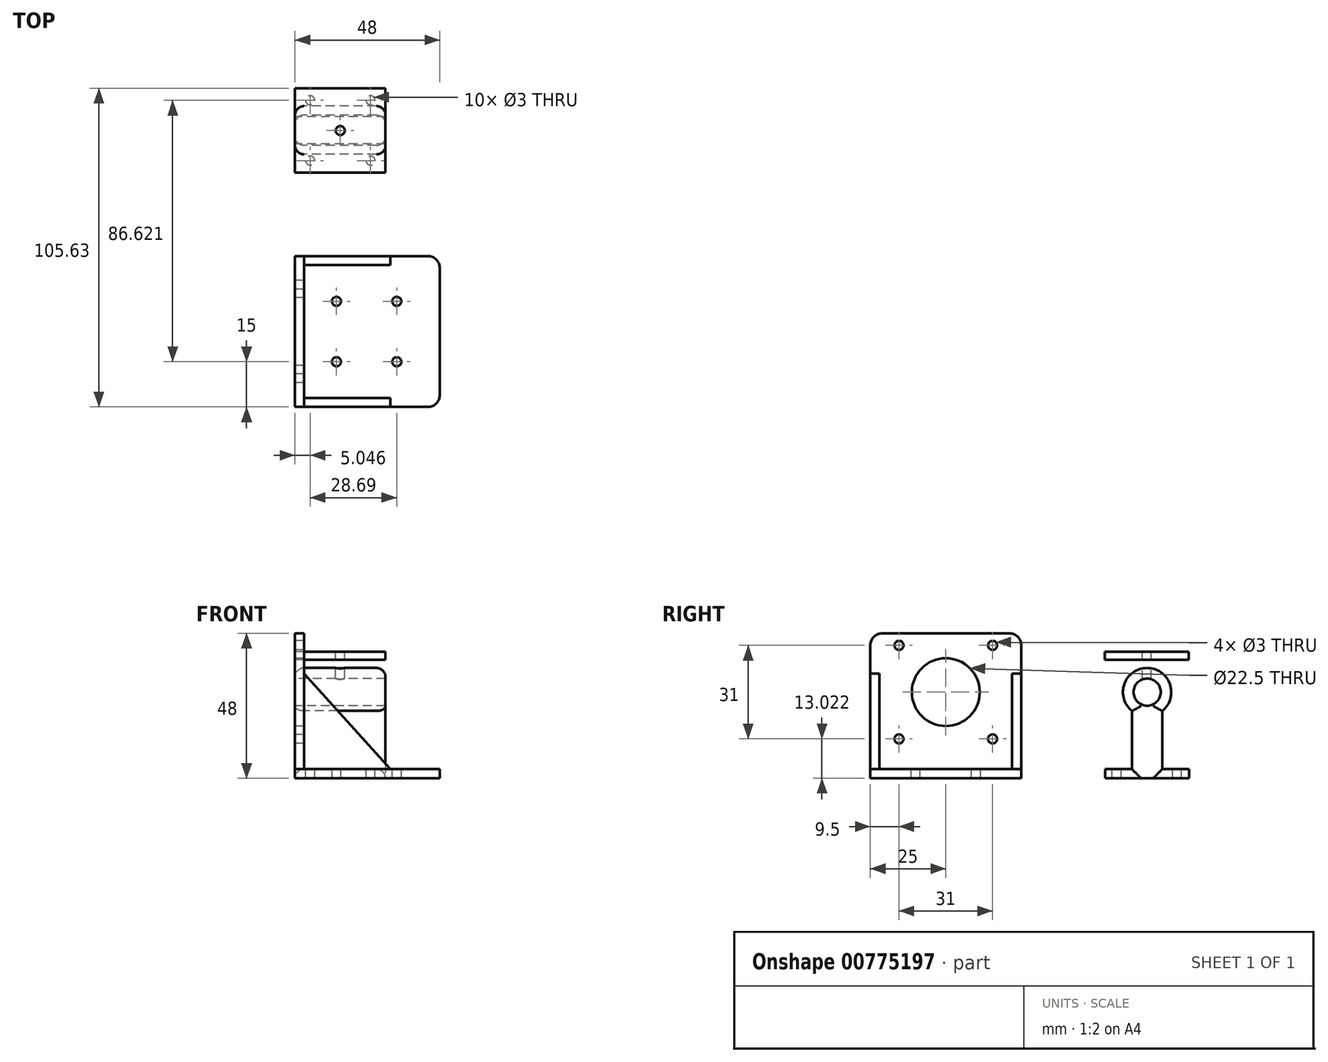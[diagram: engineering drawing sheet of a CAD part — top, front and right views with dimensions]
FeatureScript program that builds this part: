
annotation { "Feature Type Name" : "Feature", "Feature Type Description" : "" }
export const myFeature = defineFeature(function(context is Context, id is Id, definition is map)
    precondition{}
    {
        {
            var Q0;
            Q0=qCreatedBy(makeId("Right.planeOp"),FACE);
            var sketch = newSketch(context, id + "F0", { "sketchPlane" : qUnion([Q0])});
            skLineSegment(sketch, "E0.bottom", {"start": v(-50, 48) * mm, "end": v(0, 48) * mm});
            skLineSegment(sketch, "E0.top", {"start": v(-50, 0) * mm, "end": v(0, 0) * mm});
            skLineSegment(sketch, "E0.left", {"start": v(-50, 48) * mm, "end": v(-50, 0) * mm});
            skLineSegment(sketch, "E0.right", {"start": v(0, 48) * mm, "end": v(0, 0) * mm});
            skLineSegment(sketch, "E1.bottom", {"start": v(-46, 48) * mm, "end": v(-4, 48) * mm, "construction": true});
            skLineSegment(sketch, "E1.top", {"start": v(-46, 9.04) * mm, "end": v(-4, 9.04) * mm, "construction": true});
            skLineSegment(sketch, "E1.left", {"start": v(-46, 48) * mm, "end": v(-46, 9.04) * mm, "construction": true});
            skLineSegment(sketch, "E1.right", {"start": v(-4, 48) * mm, "end": v(-4, 9.04) * mm, "construction": true});
            skPoint(sketch, "E2", {"position": v(-25, 48) * mm});
            skLineSegment(sketch, "E3.bottom", {"start": v(-40.5, 44.02) * mm, "end": v(-9.5, 44.02) * mm, "construction": true});
            skLineSegment(sketch, "E3.top", {"start": v(-40.5, 13.02) * mm, "end": v(-9.5, 13.02) * mm, "construction": true});
            skLineSegment(sketch, "E3.left", {"start": v(-40.5, 44.02) * mm, "end": v(-40.5, 13.02) * mm, "construction": true});
            skLineSegment(sketch, "E3.right", {"start": v(-9.5, 44.02) * mm, "end": v(-9.5, 13.02) * mm, "construction": true});
            skPoint(sketch, "E4", {"position": v(-25, 44.02) * mm});
            skLineSegment(sketch, "E5", {"start": v(-40.5, 44.02) * mm, "end": v(-9.5, 13.02) * mm, "construction": true});
            skLineSegment(sketch, "E6", {"start": v(-9.5, 44.02) * mm, "end": v(-40.5, 13.02) * mm, "construction": true});
            skPoint(sketch, "E7", {"position": v(-25, 28.52) * mm});
            skLineSegment(sketch, "E8.top", {"start": v(-50, 3) * mm, "end": v(0, 3) * mm});
            skLineSegment(sketch, "E8.left", {"start": v(-50, 0) * mm, "end": v(-50, 3) * mm});
            skLineSegment(sketch, "E8.right", {"start": v(0, 0) * mm, "end": v(0, 3) * mm});
            skLineSegment(sketch, "E9", {"start": v(-25, 28.52) * mm, "end": v(41.7, 28.52) * mm, "construction": true});
            skCircle(sketch, "E10", {"center": v(41.7, 28.52) * mm, "radius": 8 * mm});
            skCircle(sketch, "E11", {"center": v(41.7, 28.52) * mm, "radius": 4.5 * mm});
            skLineSegment(sketch, "E12", {"start": v(41.7, 44.02) * mm, "end": v(41.7, 0) * mm, "construction": true});
            skLineSegment(sketch, "E13", {"start": v(36.7, 22.29) * mm, "end": v(36.7, 3) * mm});
            skLineSegment(sketch, "E14.left", {"start": v(41.7, 0) * mm, "end": v(41.7, 0) * mm});
            skLineSegment(sketch, "E15.bottom", {"start": v(41.7, 0) * mm, "end": v(27.8, 0) * mm});
            skLineSegment(sketch, "E15.top", {"start": v(41.7, 3) * mm, "end": v(27.8, 3) * mm});
            skLineSegment(sketch, "E15.left", {"start": v(41.7, 0) * mm, "end": v(41.7, 3) * mm});
            skLineSegment(sketch, "E15.right", {"start": v(27.8, 0) * mm, "end": v(27.8, 3) * mm});
            skLineSegment(sketch, "E16.MirrorCS", {"start": v(41.7, 0) * mm, "end": v(55.63, 0) * mm});
            skLineSegment(sketch, "E17.MirrorCS", {"start": v(55.63, 0) * mm, "end": v(55.63, 3) * mm});
            skLineSegment(sketch, "E18.MirrorCS", {"start": v(46.72, 22.29) * mm, "end": v(46.72, 3) * mm});
            skLineSegment(sketch, "E19.MirrorCS", {"start": v(41.7, 3) * mm, "end": v(55.63, 3) * mm});
            skLineSegment(sketch, "E20", {"start": v(28.63, 36.52) * mm, "end": v(60.63, 36.52) * mm, "construction": true});
            skLineSegment(sketch, "E21.bottom", {"start": v(27.65, 41.96) * mm, "end": v(55.54, 41.96) * mm});
            skLineSegment(sketch, "E21.top", {"start": v(27.65, 39.23) * mm, "end": v(55.54, 39.23) * mm});
            skLineSegment(sketch, "E21.left", {"start": v(27.65, 41.96) * mm, "end": v(27.65, 39.23) * mm});
            skLineSegment(sketch, "E21.right", {"start": v(55.54, 41.96) * mm, "end": v(55.54, 39.23) * mm});
            skSolve(sketch);
        }
        {
            var Q0;
            {var subQ0=sQuery(id+"F0.wireOp",EDGE,"E0.bottom");Q0=makeQuery(id+"F0.imprint","IMPRINT",FACE,{"disambiguationData":[TD([[makeQuery(id+"F0.imprint","IMPRINT",EDGE,{"derivedFrom":subQ0}),-1.0]])]});}
            extrude(context, id + "F1", {"entities" : qUnion([Q0]), "depth" : 3 * mm, "offsetDistance" : 25 * mm});
        }
        {
            var Q0;
            Q0=sQuery(id+"F0.wireOp",VERTEX,"E3.bottom.start");
            var Q1;
            Q1=sQuery(id+"F0.wireOp",VERTEX,"E3.bottom.end");
            var Q2;
            Q2=sQuery(id+"F0.wireOp",VERTEX,"E3.top.end");
            var Q3;
            Q3=sQuery(id+"F0.wireOp",VERTEX,"E3.top.start");
            var Q4;
            Q4=makeQuery(id+"F1.opExtrude","SWEPT_BODY",BODY,{"disambiguationData":[OSD([sQuery(id+"F0.wireOp",EDGE,"E0.bottom"),sQuery(id+"F0.wireOp",EDGE,"E0.left"),sQuery(id+"F0.wireOp",EDGE,"E0.right"),sQuery(id+"F0.wireOp",EDGE,"E8.top")])]});
            hole(context, id + "F2", {"style" : HoleStyle.SIMPLE, "endStyle" : HoleEndStyle.BLIND, "oppositeDirection" : true, "holeDiameter" : 3 * mm, "majorDiameter" : 5 * mm, "holeDepth" : 3 * mm, "isTappedThrough" : true, "tappedDepth" : 12 * mm, "tapClearance" : 3, "locations" : qUnion([Q0, Q1, Q2, Q3]), "scope" : qUnion([Q4])});
        }
        {
            var Q0;
            Q0=sQuery(id+"F0.wireOp",VERTEX,"E7");
            var Q1;
            Q1=makeQuery(id+"F1.opExtrude","SWEPT_BODY",BODY,{"disambiguationData":[OSD([sQuery(id+"F0.wireOp",EDGE,"E0.bottom"),sQuery(id+"F0.wireOp",EDGE,"E0.left"),sQuery(id+"F0.wireOp",EDGE,"E0.right"),sQuery(id+"F0.wireOp",EDGE,"E8.top")])]});
            hole(context, id + "F3", {"style" : HoleStyle.SIMPLE, "endStyle" : HoleEndStyle.BLIND, "oppositeDirection" : true, "holeDiameter" : 22.5 * mm, "majorDiameter" : 5 * mm, "holeDepth" : 3 * mm, "isTappedThrough" : true, "tappedDepth" : 12 * mm, "tapClearance" : 3, "locations" : qUnion([Q0]), "scope" : qUnion([Q1])});
        }
        {
            var Q0;
            {var subQ0=sQuery(id+"F0.wireOp",EDGE,"E0.top");Q0=makeQuery(id+"F0.imprint","IMPRINT",FACE,{"disambiguationData":[TD([[makeQuery(id+"F0.imprint","IMPRINT",EDGE,{"derivedFrom":subQ0}),1.0]])]});}
            extrude(context, id + "F4", {"entities" : qUnion([Q0]), "depth" : 48 * mm, "offsetDistance" : 25 * mm});
        }
        {
            var Q0;
            Q0=makeQuery(id+"F1.opExtrude","SWEPT_FACE",FACE,{"disambiguationData":[OSD([sQuery(id+"F0.wireOp",EDGE,"E0.right")])]});
            var sketch = newSketch(context, id + "F5", { "sketchPlane" : qUnion([Q0])});
            skPoint(sketch, "E22", {"position": v(-3, 34.6) * mm});
            skPoint(sketch, "E23", {"position": v(-31.66, 3) * mm});
            skLineSegment(sketch, "E24", {"start": v(-31.66, 3) * mm, "end": v(-3, 34.6) * mm});
            skLineSegment(sketch, "E25", {"start": v(-31.66, 3) * mm, "end": v(-3, 3) * mm});
            skLineSegment(sketch, "E26", {"start": v(-3, 3) * mm, "end": v(-3, 34.6) * mm});
            skSolve(sketch);
        }
        {
            var Q0;
            Q0=makeQuery(id+"F5.imprint","IMPRINT",FACE,{"disambiguationData":[TD([[makeQuery(id+"F5.imprint","IMPRINT",EDGE,{"derivedFrom":sQuery(id+"F5.wireOp",EDGE,"E24")}),-1.0]])]});
            extrude(context, id + "F6", {"entities" : qUnion([Q0]), "depth" : -3 * mm, "offsetDistance" : 25 * mm});
        }
        {
            var Q0;
            Q0=makeQuery(id+"F6.opExtrude","SWEPT_BODY",BODY,{"disambiguationData":[OSD([sQuery(id+"F5.wireOp",EDGE,"E24"),sQuery(id+"F5.wireOp",EDGE,"E25"),sQuery(id+"F5.wireOp",EDGE,"E26")])]});
            transform(context, id + "F7", {"entities" : qUnion([Q0]), "transformType" : TransformType.TRANSLATION_3D, "dx" : 0 * mm, "dy" : -47 * mm, "dz" : 0 * mm, "makeCopy" : true});
        }
        {
            var Q0;
            Q0=makeQuery(id+"F4.opExtrude","SWEPT_FACE",FACE,{"disambiguationData":[OSD([sQuery(id+"F0.wireOp",EDGE,"E8.top")])]});
            var sketch = newSketch(context, id + "F8", { "sketchPlane" : qUnion([Q0])});
            skLineSegment(sketch, "E27.bottom", {"start": v(13.74, -15) * mm, "end": v(33.74, -15) * mm, "construction": true});
            skLineSegment(sketch, "E27.top", {"start": v(13.74, -35) * mm, "end": v(33.74, -35) * mm, "construction": true});
            skLineSegment(sketch, "E27.left", {"start": v(13.74, -15) * mm, "end": v(13.74, -35) * mm, "construction": true});
            skLineSegment(sketch, "E27.right", {"start": v(33.74, -15) * mm, "end": v(33.74, -35) * mm, "construction": true});
            skPoint(sketch, "E28", {"position": v(33.74, -25) * mm});
            skPoint(sketch, "E29", {"position": v(48, -25) * mm});
            skPoint(sketch, "E30", {"position": v(23.74, -15) * mm});
            skLineSegment(sketch, "E31", {"start": v(48, -25) * mm, "end": v(0, -25) * mm, "construction": true});
            skSolve(sketch);
        }
        {
            var Q0;
            Q0=sQuery(id+"F8.wireOp",VERTEX,"E27.bottom.end");
            var Q1;
            Q1=sQuery(id+"F8.wireOp",VERTEX,"E27.bottom.start");
            var Q2;
            Q2=sQuery(id+"F8.wireOp",VERTEX,"E27.top.start");
            var Q3;
            Q3=sQuery(id+"F8.wireOp",VERTEX,"E27.top.end");
            var Q4;
            Q4=makeQuery(id+"F4.opExtrude","SWEPT_BODY",BODY,{"disambiguationData":[OSD([sQuery(id+"F0.wireOp",EDGE,"E0.top"),sQuery(id+"F0.wireOp",EDGE,"E0.left"),sQuery(id+"F0.wireOp",EDGE,"E0.right"),sQuery(id+"F0.wireOp",EDGE,"E8.top")])]});
            hole(context, id + "F9", {"style" : HoleStyle.SIMPLE, "endStyle" : HoleEndStyle.BLIND, "holeDiameter" : 3 * mm, "majorDiameter" : 5 * mm, "holeDepth" : 3 * mm, "isTappedThrough" : true, "tappedDepth" : 12 * mm, "tapClearance" : 3, "locations" : qUnion([Q0, Q1, Q2, Q3]), "scope" : qUnion([Q4])});
        }
        {
            var Q0;
            Q0=makeQuery(id+"F1.opExtrude","SWEPT_EDGE",EDGE,{"disambiguationData":[OSD([sQuery(id+"F0.wireOp",EDGE,"E0.bottom"),sQuery(id+"F0.wireOp",EDGE,"E0.left")])]});
            var Q1;
            Q1=makeQuery(id+"F1.opExtrude","SWEPT_EDGE",EDGE,{"disambiguationData":[OSD([sQuery(id+"F0.wireOp",EDGE,"E0.bottom"),sQuery(id+"F0.wireOp",EDGE,"E0.right")])]});
            var Q2;
            Q2=makeQuery(id+"F4.opExtrude","CAP_EDGE",EDGE,{"disambiguationData":[OSD([sQuery(id+"F0.wireOp",EDGE,"E0.left")])],"isStart":false});
            var Q3;
            Q3=makeQuery(id+"F4.opExtrude","CAP_EDGE",EDGE,{"disambiguationData":[OSD([sQuery(id+"F0.wireOp",EDGE,"E0.right")])],"isStart":false});
            fillet(context, id + "F10", {"entities" : qUnion([Q0, Q1, Q2, Q3]), "radius" : 4 * mm, "tangentPropagation" : true, "allowEdgeOverflow" : false});
        }
        {
            var Q0;
            Q0=makeQuery(id+"F0.imprint","IMPRINT",FACE,{"disambiguationData":[TD([[makeQuery(id+"F0.imprint","IMPRINT",EDGE,{"derivedFrom":sQuery(id+"F0.wireOp",EDGE,"E11")}),-1.0]])]});
            var Q1;
            {var subQ0=sQuery(id+"F0.wireOp",EDGE,"E13");Q1=makeQuery(id+"F0.imprint","IMPRINT",FACE,{"disambiguationData":[TD([[makeQuery(id+"F0.imprint","IMPRINT",EDGE,{"derivedFrom":subQ0}),1.0]])]});}
            var Q2;
            Q2=makeQuery(id+"F0.imprint","IMPRINT",FACE,{"disambiguationData":[TD([[makeQuery(id+"F0.imprint","IMPRINT",EDGE,{"derivedFrom":sQuery(id+"F0.wireOp",EDGE,"E15.bottom")}),-1.0]])]});
            var Q3;
            {var subQ3=sQuery(id+"F0.wireOp",EDGE,"E15.left");Q3=makeQuery(id+"F0.imprint","IMPRINT",FACE,{"disambiguationData":[TD([[makeQuery(id+"F0.imprint","IMPRINT",EDGE,{"derivedFrom":subQ3}),-1.0]])]});}
            extrude(context, id + "F11", {"entities" : qUnion([Q0, Q1, Q2, Q3]), "depth" : 30 * mm, "offsetDistance" : 25 * mm});
        }
        {
            var Q0;
            Q0=makeQuery(id+"F11.opExtrude","SWEPT_FACE",FACE,{"disambiguationData":[OSD([sQuery(id+"F0.wireOp",EDGE,"E19.MirrorCS")])]});
            var sketch = newSketch(context, id + "F12", { "sketchPlane" : qUnion([Q0])});
            skPoint(sketch, "E32.firstSnap0", {"position": v(0, 51.62) * mm});
            skLineSegment(sketch, "E32.bottom", {"start": v(5.05, 51.62) * mm, "end": v(25.05, 51.62) * mm, "construction": true});
            skLineSegment(sketch, "E32.top", {"start": v(5.05, 31.62) * mm, "end": v(25.05, 31.62) * mm, "construction": true});
            skLineSegment(sketch, "E32.left", {"start": v(5.05, 51.62) * mm, "end": v(5.05, 31.62) * mm, "construction": true});
            skLineSegment(sketch, "E32.right", {"start": v(25.05, 51.62) * mm, "end": v(25.05, 31.62) * mm, "construction": true});
            skSolve(sketch);
        }
        {
            var Q0;
            Q0=sQuery(id+"F12.wireOp",VERTEX,"E32.bottom.start");
            var Q1;
            Q1=sQuery(id+"F12.wireOp",VERTEX,"E32.bottom.end");
            var Q2;
            Q2=sQuery(id+"F12.wireOp",VERTEX,"E32.top.end");
            var Q3;
            Q3=sQuery(id+"F12.wireOp",VERTEX,"E32.top.start");
            var Q4;
            Q4=makeQuery(id+"F11.opExtrude","SWEPT_BODY",BODY,{"disambiguationData":[OSD([sQuery(id+"F0.wireOp",EDGE,"E10"),sQuery(id+"F0.wireOp",EDGE,"E11"),sQuery(id+"F0.wireOp",EDGE,"E13"),sQuery(id+"F0.wireOp",EDGE,"E15.bottom"),sQuery(id+"F0.wireOp",EDGE,"E15.top"),sQuery(id+"F0.wireOp",EDGE,"E15.right"),sQuery(id+"F0.wireOp",EDGE,"E16.MirrorCS"),sQuery(id+"F0.wireOp",EDGE,"E17.MirrorCS"),sQuery(id+"F0.wireOp",EDGE,"E18.MirrorCS"),sQuery(id+"F0.wireOp",EDGE,"E19.MirrorCS")])]});
            hole(context, id + "F13", {"style" : HoleStyle.SIMPLE, "endStyle" : HoleEndStyle.BLIND, "holeDiameter" : 3 * mm, "majorDiameter" : 5 * mm, "holeDepth" : 3 * mm, "isTappedThrough" : true, "tappedDepth" : 12 * mm, "tapClearance" : 3, "locations" : qUnion([Q0, Q1, Q2, Q3]), "scope" : qUnion([Q4])});
        }
        {
            var Q0;
            Q0=makeQuery(id+"F11.opExtrude","CAP_EDGE",EDGE,{"disambiguationData":[OSD([sQuery(id+"F0.wireOp",EDGE,"E10")])],"isStart":false});
            var Q1;
            Q1=makeQuery(id+"F11.opExtrude","CAP_EDGE",EDGE,{"disambiguationData":[OSD([sQuery(id+"F0.wireOp",EDGE,"E13")])],"isStart":false});
            var Q2;
            Q2=makeQuery(id+"F11.opExtrude","CAP_EDGE",EDGE,{"disambiguationData":[OSD([sQuery(id+"F0.wireOp",EDGE,"E18.MirrorCS")])],"isStart":false});
            var Q3;
            Q3=makeQuery(id+"F11.opExtrude","CAP_EDGE",EDGE,{"disambiguationData":[OSD([sQuery(id+"F0.wireOp",EDGE,"E19.MirrorCS")])],"isStart":false});
            var Q4;
            Q4=makeQuery(id+"F11.opExtrude","CAP_EDGE",EDGE,{"disambiguationData":[OSD([sQuery(id+"F0.wireOp",EDGE,"E15.top")])],"isStart":false});
            var Q5;
            Q5=makeQuery(id+"F11.opExtrude","CAP_EDGE",EDGE,{"disambiguationData":[OSD([sQuery(id+"F0.wireOp",EDGE,"E10")])],"isStart":true});
            var Q6;
            Q6=makeQuery(id+"F11.opExtrude","CAP_EDGE",EDGE,{"disambiguationData":[OSD([sQuery(id+"F0.wireOp",EDGE,"E13")])],"isStart":true});
            var Q7;
            Q7=makeQuery(id+"F11.opExtrude","CAP_EDGE",EDGE,{"disambiguationData":[OSD([sQuery(id+"F0.wireOp",EDGE,"E18.MirrorCS")])],"isStart":true});
            var Q8;
            Q8=makeQuery(id+"F11.opExtrude","CAP_EDGE",EDGE,{"disambiguationData":[OSD([sQuery(id+"F0.wireOp",EDGE,"E19.MirrorCS")])],"isStart":true});
            var Q9;
            Q9=makeQuery(id+"F11.opExtrude","CAP_EDGE",EDGE,{"disambiguationData":[OSD([sQuery(id+"F0.wireOp",EDGE,"E15.top")])],"isStart":true});
            fillet(context, id + "F14", {"entities" : qUnion([Q0, Q1, Q2, Q3, Q4, Q5, Q6, Q7, Q8, Q9]), "radius" : 3 * mm, "tangentPropagation" : true, "allowEdgeOverflow" : false});
        }
        {
            var Q0;
            Q0=makeQuery(id+"F0.imprint","IMPRINT",FACE,{"disambiguationData":[TD([[makeQuery(id+"F0.imprint","IMPRINT",EDGE,{"derivedFrom":sQuery(id+"F0.wireOp",EDGE,"E21.bottom")}),-1.0]])]});
            extrude(context, id + "F15", {"entities" : qUnion([Q0]), "depth" : 30 * mm, "offsetDistance" : 25 * mm});
        }
        {
            var Q0;
            Q0=makeQuery(id+"F15.opExtrude","SWEPT_FACE",FACE,{"disambiguationData":[OSD([sQuery(id+"F0.wireOp",EDGE,"E21.bottom")])]});
            var sketch = newSketch(context, id + "F16", { "sketchPlane" : qUnion([Q0])});
            skLineSegment(sketch, "E33", {"start": v(0, 55.54) * mm, "end": v(30, 27.65) * mm, "construction": true});
            skLineSegment(sketch, "E34", {"start": v(30, 55.54) * mm, "end": v(0, 27.65) * mm, "construction": true});
            skPoint(sketch, "E35", {"position": v(15, 41.6) * mm});
            skSolve(sketch);
        }
        {
            var Q0;
            Q0=sQuery(id+"F16.wireOp",VERTEX,"E35");
            var Q1;
            Q1=makeQuery(id+"F11.opExtrude","SWEPT_BODY",BODY,{"disambiguationData":[OSD([sQuery(id+"F0.wireOp",EDGE,"E10"),sQuery(id+"F0.wireOp",EDGE,"E11"),sQuery(id+"F0.wireOp",EDGE,"E13"),sQuery(id+"F0.wireOp",EDGE,"E15.bottom"),sQuery(id+"F0.wireOp",EDGE,"E15.top"),sQuery(id+"F0.wireOp",EDGE,"E15.right"),sQuery(id+"F0.wireOp",EDGE,"E16.MirrorCS"),sQuery(id+"F0.wireOp",EDGE,"E17.MirrorCS"),sQuery(id+"F0.wireOp",EDGE,"E18.MirrorCS"),sQuery(id+"F0.wireOp",EDGE,"E19.MirrorCS")])]});
            var Q2;
            Q2=makeQuery(id+"F15.opExtrude","SWEPT_BODY",BODY,{"disambiguationData":[OSD([sQuery(id+"F0.wireOp",EDGE,"E21.bottom"),sQuery(id+"F0.wireOp",EDGE,"E21.top"),sQuery(id+"F0.wireOp",EDGE,"E21.left"),sQuery(id+"F0.wireOp",EDGE,"E21.right")])]});
            hole(context, id + "F17", {"style" : HoleStyle.SIMPLE, "endStyle" : HoleEndStyle.BLIND, "holeDiameter" : 3 * mm, "majorDiameter" : 5 * mm, "holeDepth" : 12 * mm, "isTappedThrough" : true, "tappedDepth" : 12 * mm, "tapClearance" : 3, "locations" : qUnion([Q0]), "scope" : qUnion([Q1, Q2])});
        }
    });
